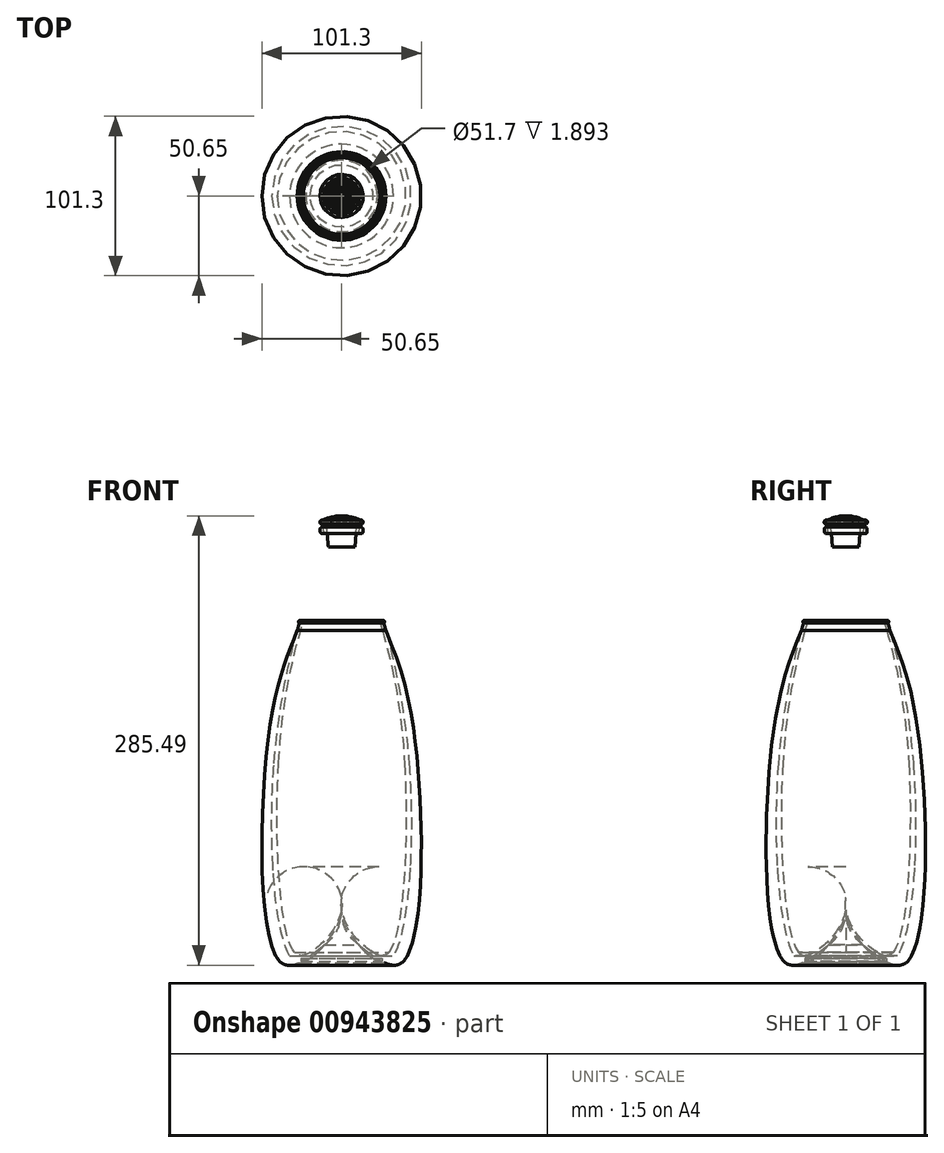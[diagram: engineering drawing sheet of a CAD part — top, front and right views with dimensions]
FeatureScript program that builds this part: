
annotation { "Feature Type Name" : "Feature", "Feature Type Description" : "" }
export const myFeature = defineFeature(function(context is Context, id is Id, definition is map)
    precondition{}
    {
        {
            var Q0;
            Q0=qCreatedBy(makeId("Front.planeOp"),FACE);
            var sketch = newSketch(context, id + "F0", { "sketchPlane" : qUnion([Q0])});
            skLineSegment(sketch, "E0", {"start": v(0, 0) * mm, "end": v(0, 270) * mm});
            skLineSegment(sketch, "E1", {"start": v(-9.5, 270) * mm, "end": v(-8.58, 259.44) * mm});
            skPoint(sketch, "E2", {"position": v(0, 246) * mm});
            skLineSegment(sketch, "E3", {"start": v(-77.67, 256) * mm, "end": v(0, 256) * mm});
            skLineSegment(sketch, "E4", {"start": v(-40, 120) * mm, "end": v(118.95, 120) * mm});
            skLineSegment(sketch, "E5", {"start": v(0, 0) * mm, "end": v(-30, 0) * mm});
            skPoint(sketch, "E6", {"position": v(0, 27) * mm});
            skLineSegment(sketch, "E7", {"start": v(-9.5, 270) * mm, "end": v(0, 270) * mm});
            skPoint(sketch, "E8", {"position": v(-20, 0) * mm});
            skFitSpline(sketch, "E9", {"points": [v(0, 27) * mm, v(-20, 0) * mm, v(-30, 0) * mm, v(-40, 120) * mm, v(-8.28, 256) * mm], "startDerivative": vector(-50.01, -221.22) * mm, "endDerivative": vector(151.7, 395.11) * mm});
            skArc(sketch, "E10.filletArc", {"start": v(-9.5, 252.8) * mm, "mid": v(-8.66, 256.07) * mm, "end": v(-8.58, 259.44) * mm});
            skLineSegment(sketch, "E11", {"start": v(0, 210) * mm, "end": v(-76.1, 210) * mm});
            skPoint(sketch, "E12", {"position": v(-24.3, 210) * mm});
            skSolve(sketch);
        }
        {
            var Q0;
            Q0=qCreatedBy(makeId("Front.planeOp"),FACE);
            var sketch = newSketch(context, id + "F1", { "sketchPlane" : qUnion([Q0])});
            skLineSegment(sketch, "E13.0.0", {"start": v(-40, 120) * mm, "end": v(-42.85, 120) * mm});
            skFitSpline(sketch, "E13.0.1", {"points": [v(-8.28, 256) * mm, v(-27.1, 206.98) * mm, v(-46.24, 138.17) * mm, v(-38.6, -6.34) * mm, v(-17.98, -0.72) * mm, v(-3.04, 13.54) * mm, v(0, 27) * mm]});
            skLineSegment(sketch, "E13.0.4", {"start": v(0, 27) * mm, "end": v(0, 120) * mm});
            skLineSegment(sketch, "E14", {"start": v(-49.37, -2.11) * mm, "end": v(37.47, -2.11) * mm});
            skPoint(sketch, "E15", {"position": v(-25.85, -2.11) * mm});
            skLineSegment(sketch, "E16", {"start": v(-25.85, -2.11) * mm, "end": v(-25.85, -31.53) * mm});
            skLineSegment(sketch, "E17", {"start": v(-45.24, -4) * mm, "end": v(-6, -4) * mm});
            skPoint(sketch, "E18", {"position": v(0, 25) * mm});
            skLineSegment(sketch, "E19.0", {"start": v(-11.5, 270) * mm, "end": v(-10.57, 259.26) * mm});
            skArc(sketch, "E20.0", {"start": v(-11.38, 253.49) * mm, "mid": v(-10.64, 256.33) * mm, "end": v(-10.57, 259.26) * mm});
            skPoint(sketch, "E21", {"position": v(-42.85, 120) * mm});
            skPoint(sketch, "E22", {"position": v(-20, -4) * mm});
            skPoint(sketch, "E23", {"position": v(-31.56, -4) * mm});
            skFitSpline(sketch, "E24", {"points": [v(0, 25) * mm, v(-20, -4) * mm, v(-31.56, -4) * mm, v(-42.85, 120) * mm, v(-11.38, 253.49) * mm], "startDerivative": vector(-33.89, -165.62) * mm, "endDerivative": vector(107.89, 254.87) * mm});
            skLineSegment(sketch, "E25.0", {"start": v(0, 210) * mm, "end": v(-26.58, 210) * mm});
            skPoint(sketch, "E26", {"position": v(-26.58, 210) * mm});
            skLineSegment(sketch, "E27.0", {"start": v(-9.45, 269.4) * mm, "end": v(-8.89, 263.03) * mm});
            skPoint(sketch, "E28.0", {"position": v(-8.28, 256) * mm});
            skArc(sketch, "E29.0", {"start": v(-9.5, 252.8) * mm, "mid": v(-8.66, 256.07) * mm, "end": v(-8.58, 259.44) * mm});
            skPoint(sketch, "E30.orphan", {"position": v(-8.58, 259.44) * mm});
            skLineSegment(sketch, "E31.0", {"start": v(-11.5, 270) * mm, "end": v(-10.1, 270) * mm});
            skPoint(sketch, "E32.orphan", {"position": v(0, 270) * mm});
            skPoint(sketch, "E33.visualSharp", {"position": v(-9.5, 270) * mm});
            skArc(sketch, "E33.filletArc", {"start": v(-9.45, 269.4) * mm, "mid": v(-9.66, 269.83) * mm, "end": v(-10.1, 270) * mm});
            skLineSegment(sketch, "E34", {"start": v(-11.5, 270) * mm, "end": v(-12.5, 270) * mm});
            skLineSegment(sketch, "E35", {"start": v(-13.5, 269) * mm, "end": v(-13.5, 267) * mm});
            skLineSegment(sketch, "E36", {"start": v(-12.5, 266) * mm, "end": v(-11.16, 266) * mm});
            skPoint(sketch, "E37.visualSharp", {"position": v(-13.5, 270) * mm});
            skArc(sketch, "E37.filletArc", {"start": v(-12.5, 270) * mm, "mid": v(-13.21, 269.7) * mm, "end": v(-13.5, 269) * mm});
            skPoint(sketch, "E38.visualSharp", {"position": v(-13.5, 266) * mm});
            skArc(sketch, "E38.filletArc", {"start": v(-13.5, 267) * mm, "mid": v(-13.21, 266.3) * mm, "end": v(-12.5, 266) * mm});
            skLineSegment(sketch, "E39", {"start": v(-8.58, 259.44) * mm, "end": v(-8.89, 263.03) * mm});
            skFitSpline(sketch, "E40.0", {"points": [v(0, 27) * mm, v(-3.04, 13.54) * mm, v(-17.98, -0.72) * mm, v(-38.6, -6.34) * mm, v(-46.24, 138.17) * mm, v(-27.1, 206.98) * mm, v(-8.28, 256) * mm]});
            skLineSegment(sketch, "E41.0", {"start": v(0, 0) * mm, "end": v(-20, 0) * mm});
            skLineSegment(sketch, "E42.0", {"start": v(0, 25) * mm, "end": v(0, 120) * mm});
            skArc(sketch, "E43", {"start": v(-26.37, 210.72) * mm, "mid": v(-27.3, 210.2) * mm, "end": v(-26.78, 209.28) * mm});
            skArc(sketch, "E44", {"start": v(-43.53, 53.66) * mm, "mid": v(-44.23, 52.87) * mm, "end": v(-43.43, 52.17) * mm});
            skLineSegment(sketch, "E45.trimOffspring", {"start": v(-27.33, 210) * mm, "end": v(-76.1, 210) * mm});
            skLineSegment(sketch, "E46.trimOffspring", {"start": v(0, 210) * mm, "end": v(0, 270) * mm});
            skPoint(sketch, "E47.orphan", {"position": v(0, 0) * mm});
            skPoint(sketch, "E48.orphan", {"position": v(-30, 0) * mm});
            skSolve(sketch);
        }
        {
            var Q0;
            {var subQ0=sQuery(id+"F0.wireOp",EDGE,"E9");var subQ6=sQuery(id+"F0.wireOp",EDGE,"E0");var subQ8=makeQuery(id+"F0.imprint","INTERSECT",VERTEX,{"derivedFrom":[subQ6,subQ0]});Q0=makeQuery(id+"F0.imprint","IMPRINT",FACE,{"disambiguationData":[TD([[makeQuery(id+"F0.imprint","IMPRINT",EDGE,{"disambiguationData":[TD([[subQ8,-1.0]])],"derivedFrom":subQ6}),1.0]])]});}
            var Q1;
            {var subQ0=sQuery(id+"F0.wireOp",EDGE,"E9");var subQ1=sQuery(id+"F0.wireOp",EDGE,"E5");var subQ2=makeQuery(id+"F0.imprint","INTERSECT",VERTEX,{"disambiguationData":[OD(0.0)],"derivedFrom":[subQ1,subQ0]});Q1=makeQuery(id+"F0.imprint","IMPRINT",FACE,{"disambiguationData":[TD([[makeQuery(id+"F0.imprint","IMPRINT",EDGE,{"disambiguationData":[TD([[subQ2,1.0]])],"derivedFrom":subQ1}),1.0]])]});}
            var Q2;
            {var subQ0=sQuery(id+"F0.wireOp",EDGE,"E11");var subQ1=sQuery(id+"F0.wireOp",EDGE,"E0");var subQ2=makeQuery(id+"F0.imprint","INTERSECT",VERTEX,{"derivedFrom":[subQ1,subQ0]});Q2=makeQuery(id+"F0.imprint","IMPRINT",FACE,{"disambiguationData":[TD([[makeQuery(id+"F0.imprint","IMPRINT",EDGE,{"disambiguationData":[TD([[subQ2,1.0]])],"derivedFrom":subQ1}),1.0]])]});}
            var Q3;
            Q3=sQuery(id+"F0.wireOp",EDGE,"E0");
            revolve(context, id + "F2", {"surfaceOperationType" : NewSurfaceOperationType.NEW, "entities" : qUnion([Q0, Q1, Q2]), "axis" : qUnion([Q3]), "revolveType" : RevolveType.FULL});
        }
        {
            var Q0;
            Q0 = qSketchRegion(id + "F1", true);
            var Q1;
            Q1=sQuery(id+"F1.wireOp",EDGE,"E13.0.4");
            revolve(context, id + "F3", {"surfaceOperationType" : NewSurfaceOperationType.NEW, "entities" : qUnion([Q0]), "axis" : qUnion([Q1]), "revolveType" : RevolveType.FULL});
        }
        {
            var Q0;
            Q0=qCreatedBy(makeId("Front.planeOp"),FACE);
            var sketch = newSketch(context, id + "F4", { "sketchPlane" : qUnion([Q0])});
            skLineSegment(sketch, "E49.0", {"start": v(-9.67, 272) * mm, "end": v(-8.4, 257.44) * mm});
            skPoint(sketch, "E50.0", {"position": v(-12.5, 267) * mm});
            skPoint(sketch, "E51.0", {"position": v(-12.5, 269) * mm});
            skLineSegment(sketch, "E52.0", {"start": v(0, 257.44) * mm, "end": v(0, 278.5) * mm});
            skLineSegment(sketch, "E53", {"start": v(-12.5, 272) * mm, "end": v(0, 272) * mm});
            skLineSegment(sketch, "E54", {"start": v(0, 257.44) * mm, "end": v(-8.4, 257.44) * mm});
            skPoint(sketch, "E55.orphan", {"position": v(0, 0) * mm});
            skCircle(sketch, "E56", {"center": v(-12.5, 273.25) * mm, "radius": 1.25 * mm});
            skArc(sketch, "E57", {"start": v(-12.5, 273.25) * mm, "mid": v(-6.46, 275.67) * mm, "end": v(0, 276.5) * mm});
            skArc(sketch, "E58", {"start": v(0, 278.5) * mm, "mid": v(-2, 276.5) * mm, "end": v(0, 274.5) * mm});
            skArc(sketch, "E59.MirrorCS", {"start": v(12.5, 273.25) * mm, "mid": v(6.46, 275.67) * mm, "end": v(0, 276.5) * mm});
            skSolve(sketch);
        }
        {
            var Q0;
            {var subQ0=sQuery(id+"F4.wireOp",EDGE,"E57");var subQ1=sQuery(id+"F4.wireOp",EDGE,"E52.0");var subQ2=makeQuery(id+"F4.imprint","INTERSECT",VERTEX,{"derivedFrom":[subQ1,subQ0]});Q0=makeQuery(id+"F4.imprint","IMPRINT",FACE,{"disambiguationData":[TD([[makeQuery(id+"F4.imprint","IMPRINT",EDGE,{"disambiguationData":[TD([[subQ2,1.0]])],"derivedFrom":subQ1}),1.0]])]});}
            var Q1;
            {var subQ1=sQuery(id+"F4.wireOp",EDGE,"E53");var subQ6=sQuery(id+"F4.wireOp",EDGE,"E52.0");var subQ7=makeQuery(id+"F4.imprint","INTERSECT",VERTEX,{"derivedFrom":[subQ6,subQ1]});Q1=makeQuery(id+"F4.imprint","IMPRINT",FACE,{"disambiguationData":[TD([[makeQuery(id+"F4.imprint","IMPRINT",EDGE,{"disambiguationData":[TD([[subQ7,-1.0]])],"derivedFrom":subQ6}),1.0]])]});}
            var Q2;
            {var subQ0=sQuery(id+"F4.wireOp",EDGE,"E56");var subQ1=makeQuery(id+"F4.imprint","INTERSECT",VERTEX,{"derivedFrom":[sQuery(id+"F4.wireOp",EDGE,"E53"),subQ0]});Q2=makeQuery(id+"F4.imprint","IMPRINT",FACE,{"disambiguationData":[TD([[makeQuery(id+"F4.imprint","IMPRINT",EDGE,{"disambiguationData":[TD([[subQ1,1.0]])],"derivedFrom":subQ0}),1.0]])]});}
            var Q3;
            Q3=sQuery(id+"F4.wireOp",EDGE,"E52.0");
            revolve(context, id + "F5", {"surfaceOperationType" : NewSurfaceOperationType.NEW, "entities" : qUnion([Q0, Q1, Q2]), "axis" : qUnion([Q3]), "revolveType" : RevolveType.FULL});
        }
        {
            var Q0;
            {var subQ0=sQuery(id+"F4.wireOp",EDGE,"E49.0");Q0=makeQuery(id+"F4.imprint","IMPRINT",FACE,{"disambiguationData":[TD([[makeQuery(id+"F4.imprint","IMPRINT",EDGE,{"derivedFrom":subQ0}),1.0]])]});}
            var Q1;
            Q1=sQuery(id+"F4.wireOp",EDGE,"E52.0");
            revolve(context, id + "F6", {"surfaceOperationType" : NewSurfaceOperationType.NEW, "entities" : qUnion([Q0]), "axis" : qUnion([Q1]), "revolveType" : RevolveType.FULL});
        }
        {
            var Q0;
            Q0=qCreatedBy(makeId("Right.planeOp"),FACE);
            var sketch = newSketch(context, id + "F7", { "sketchPlane" : qUnion([Q0])});
            skLineSegment(sketch, "E60.0", {"start": v(0, 273.25) * mm, "end": v(0, 276.5) * mm});
            skLineSegment(sketch, "E61.0", {"start": v(0, 257.44) * mm, "end": v(0, 278.5) * mm});
            skCircle(sketch, "E62", {"center": v(0, 276.5) * mm, "radius": 0.75 * mm});
            skArc(sketch, "E63", {"start": v(11.4, 273.83) * mm, "mid": v(0, 276.5) * mm, "end": v(-11.4, 273.83) * mm});
            skArc(sketch, "E64", {"start": v(-0.75, 276.49) * mm, "mid": v(-0.46, 276.95) * mm, "end": v(0, 277.25) * mm});
            skPoint(sketch, "E65", {"position": v(0, 277.25) * mm});
            skPoint(sketch, "E66", {"position": v(-0.75, 276.49) * mm});
            skArc(sketch, "E67.MirrorCS", {"start": v(0.75, 276.49) * mm, "mid": v(0.46, 276.95) * mm, "end": v(0, 277.25) * mm});
            skSolve(sketch);
        }
        {
            var Q0;
            {var subQ0=sQuery(id+"F7.wireOp",EDGE,"E60.0");var subQ1=sQuery(id+"F7.wireOp",EDGE,"E61.0");var subQ2=makeQuery(id+"F7.imprint","INTERSECT",VERTEX,{"derivedFrom":[subQ1,subQ0]});Q0=makeQuery(id+"F7.imprint","IMPRINT",FACE,{"disambiguationData":[TD([[makeQuery(id+"F7.imprint","IMPRINT",EDGE,{"disambiguationData":[TD([[subQ2,-1.0]])],"derivedFrom":subQ1}),-1.0]])]});}
            var Q1;
            {var subQ0=sQuery(id+"F7.wireOp",EDGE,"E60.0");var subQ1=sQuery(id+"F7.wireOp",EDGE,"E61.0");var subQ2=makeQuery(id+"F7.imprint","INTERSECT",VERTEX,{"derivedFrom":[subQ1,subQ0]});Q1=makeQuery(id+"F7.imprint","IMPRINT",FACE,{"disambiguationData":[TD([[makeQuery(id+"F7.imprint","IMPRINT",EDGE,{"disambiguationData":[TD([[subQ2,-1.0]])],"derivedFrom":subQ1}),1.0]])]});}
            var Q2;
            Q2=sQuery(id+"F4.wireOp",EDGE,"E57");
            var Q3;
            Q3=sQuery(id+"F4.wireOp",EDGE,"E59.MirrorCS");
            sweep(context, id + "F8", {"profiles" : qUnion([Q0, Q1]), "path" : qUnion([Q2, Q3])});
        }
        {
            var Q0;
            Q0=makeQuery(id+"F8.opSweep","SWEPT_BODY",BODY,{"disambiguationData":[OSD([sQuery(id+"F4.wireOp",EDGE,"E59.MirrorCS"),sQuery(id+"F7.wireOp",EDGE,"E63"),sQuery(id+"F7.wireOp",EDGE,"E64"),sQuery(id+"F7.wireOp",EDGE,"E67.MirrorCS")])]});
            var Q1;
            Q1=sQuery(id+"F7.wireOp",EDGE,"E61.0");
            transform(context, id + "F9", {"entities" : qUnion([Q0]), "transformType" : TransformType.ROTATION, "transformAxis" : qUnion([Q1]), "angle" : 20 * degree, "makeCopy" : true});
        }
        {
            var Q0;
            Q0=makeQuery(id+"F8.opSweep","SWEPT_BODY",BODY,{"disambiguationData":[OSD([sQuery(id+"F4.wireOp",EDGE,"E59.MirrorCS"),sQuery(id+"F7.wireOp",EDGE,"E63"),sQuery(id+"F7.wireOp",EDGE,"E64"),sQuery(id+"F7.wireOp",EDGE,"E67.MirrorCS")])]});
            var Q1;
            Q1=sQuery(id+"F7.wireOp",EDGE,"E61.0");
            transform(context, id + "F10", {"entities" : qUnion([Q0]), "transformType" : TransformType.ROTATION, "transformAxis" : qUnion([Q1]), "angle" : 40 * degree, "makeCopy" : true});
        }
        {
            var Q0;
            Q0=makeQuery(id+"F8.opSweep","SWEPT_BODY",BODY,{"disambiguationData":[OSD([sQuery(id+"F4.wireOp",EDGE,"E59.MirrorCS"),sQuery(id+"F7.wireOp",EDGE,"E63"),sQuery(id+"F7.wireOp",EDGE,"E64"),sQuery(id+"F7.wireOp",EDGE,"E67.MirrorCS")])]});
            var Q1;
            Q1=sQuery(id+"F7.wireOp",EDGE,"E61.0");
            transform(context, id + "F11", {"entities" : qUnion([Q0]), "transformType" : TransformType.ROTATION, "transformAxis" : qUnion([Q1]), "angle" : 60 * degree, "makeCopy" : true});
        }
        {
            var Q0;
            Q0=makeQuery(id+"F8.opSweep","SWEPT_BODY",BODY,{"disambiguationData":[OSD([sQuery(id+"F4.wireOp",EDGE,"E59.MirrorCS"),sQuery(id+"F7.wireOp",EDGE,"E63"),sQuery(id+"F7.wireOp",EDGE,"E64"),sQuery(id+"F7.wireOp",EDGE,"E67.MirrorCS")])]});
            var Q1;
            Q1=sQuery(id+"F7.wireOp",EDGE,"E61.0");
            transform(context, id + "F12", {"entities" : qUnion([Q0]), "transformType" : TransformType.ROTATION, "transformAxis" : qUnion([Q1]), "angle" : 80 * degree, "makeCopy" : true});
        }
        {
            var Q0;
            Q0=makeQuery(id+"F8.opSweep","SWEPT_BODY",BODY,{"disambiguationData":[OSD([sQuery(id+"F4.wireOp",EDGE,"E59.MirrorCS"),sQuery(id+"F7.wireOp",EDGE,"E63"),sQuery(id+"F7.wireOp",EDGE,"E64"),sQuery(id+"F7.wireOp",EDGE,"E67.MirrorCS")])]});
            var Q1;
            Q1=sQuery(id+"F7.wireOp",EDGE,"E61.0");
            transform(context, id + "F13", {"entities" : qUnion([Q0]), "transformType" : TransformType.ROTATION, "transformAxis" : qUnion([Q1]), "angle" : 100 * degree, "makeCopy" : true});
        }
        {
            var Q0;
            Q0=makeQuery(id+"F8.opSweep","SWEPT_BODY",BODY,{"disambiguationData":[OSD([sQuery(id+"F4.wireOp",EDGE,"E59.MirrorCS"),sQuery(id+"F7.wireOp",EDGE,"E63"),sQuery(id+"F7.wireOp",EDGE,"E64"),sQuery(id+"F7.wireOp",EDGE,"E67.MirrorCS")])]});
            var Q1;
            Q1=sQuery(id+"F7.wireOp",EDGE,"E61.0");
            transform(context, id + "F14", {"entities" : qUnion([Q0]), "transformType" : TransformType.ROTATION, "transformAxis" : qUnion([Q1]), "angle" : 120 * degree, "makeCopy" : true});
        }
        {
            var Q0;
            Q0=makeQuery(id+"F8.opSweep","SWEPT_BODY",BODY,{"disambiguationData":[OSD([sQuery(id+"F4.wireOp",EDGE,"E59.MirrorCS"),sQuery(id+"F7.wireOp",EDGE,"E63"),sQuery(id+"F7.wireOp",EDGE,"E64"),sQuery(id+"F7.wireOp",EDGE,"E67.MirrorCS")])]});
            var Q1;
            Q1=sQuery(id+"F7.wireOp",EDGE,"E61.0");
            transform(context, id + "F15", {"entities" : qUnion([Q0]), "transformType" : TransformType.ROTATION, "transformAxis" : qUnion([Q1]), "angle" : 140 * degree, "makeCopy" : true});
        }
        {
            var Q0;
            Q0=makeQuery(id+"F8.opSweep","SWEPT_BODY",BODY,{"disambiguationData":[OSD([sQuery(id+"F4.wireOp",EDGE,"E59.MirrorCS"),sQuery(id+"F7.wireOp",EDGE,"E63"),sQuery(id+"F7.wireOp",EDGE,"E64"),sQuery(id+"F7.wireOp",EDGE,"E67.MirrorCS")])]});
            var Q1;
            Q1=sQuery(id+"F7.wireOp",EDGE,"E61.0");
            transform(context, id + "F16", {"entities" : qUnion([Q0]), "transformType" : TransformType.ROTATION, "transformAxis" : qUnion([Q1]), "angle" : 160 * degree, "makeCopy" : true});
        }
    });
